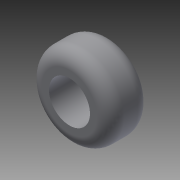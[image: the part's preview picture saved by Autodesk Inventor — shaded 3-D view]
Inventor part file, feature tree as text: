
AUTODESK INVENTOR PART (.ipt)
format: ipt  version: 2014 SP2 (Build 180246200, 246)  size: 126,976 bytes
history: native  units: mm
features: extrude x1, fillet x1, sketch x1
ambient origin geometry x8: Origin, YZ Plane, XZ Plane, XY Plane, X Axis, Y Axis, Z Axis, Center Point
bodies: Solid1 (feature_tree)
feature tree (3):
  extrude  "Extrusion1"  Depth=1.0mm
  fillet  "Fillet1"  Radius=3.0mm
  sketch  "Sketch1"  dims[d0=3.0mm d1=6.0mm d2=3.0mm d3=0.0mm d4=1.0mm]
